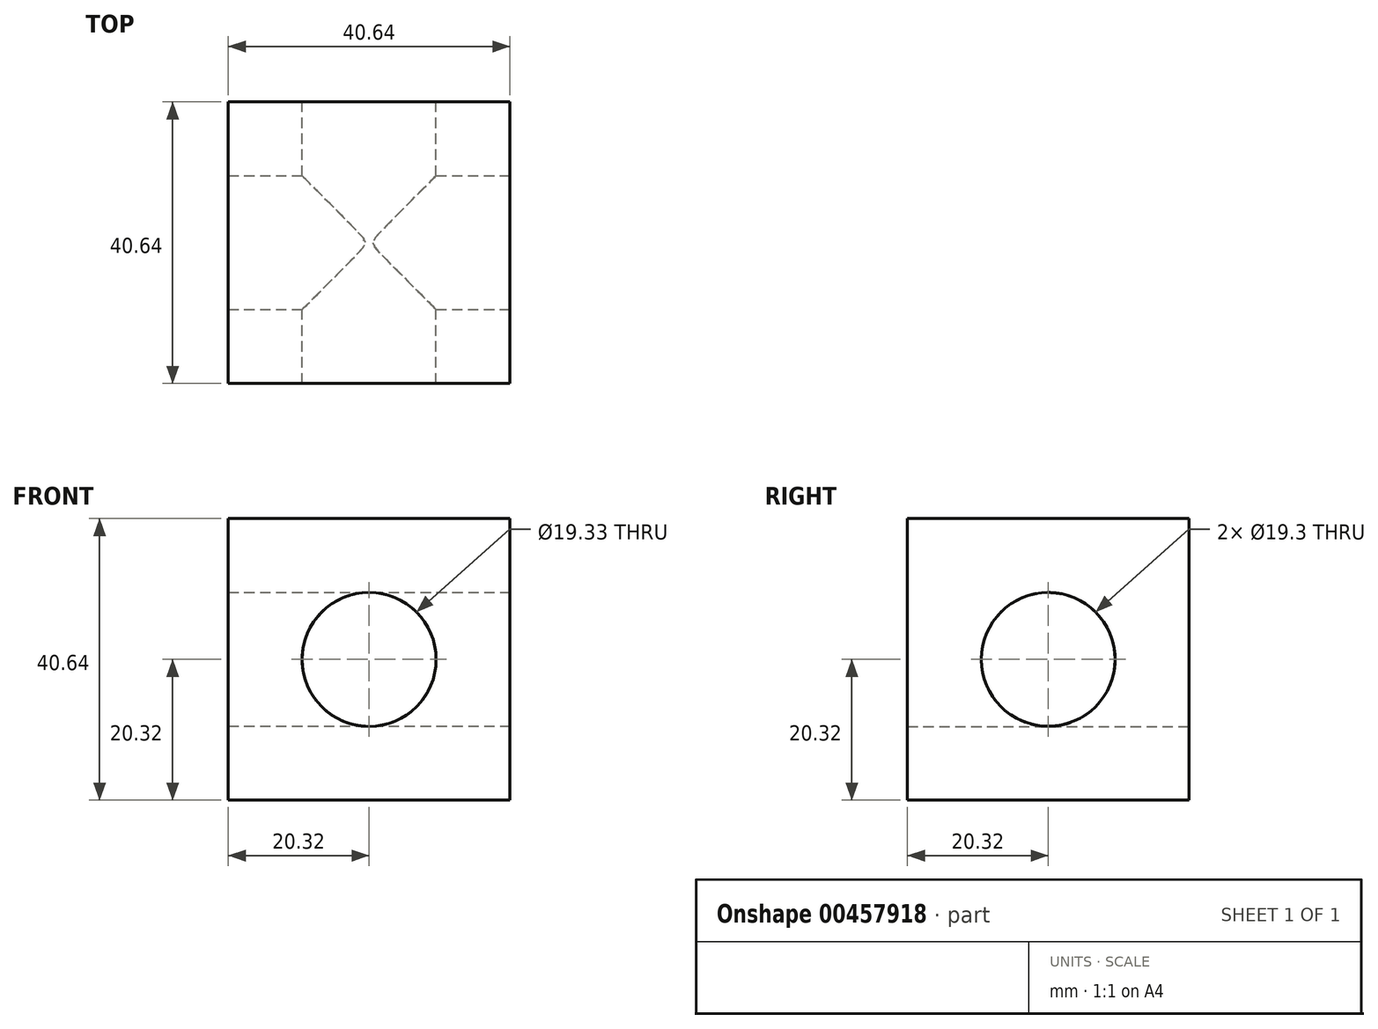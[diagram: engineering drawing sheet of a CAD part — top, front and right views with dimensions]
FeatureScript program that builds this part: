
annotation { "Feature Type Name" : "Feature", "Feature Type Description" : "" }
export const myFeature = defineFeature(function(context is Context, id is Id, definition is map)
    precondition{}
    {
        {
            var Q0;
            Q0=qCreatedBy(makeId("Front.planeOp"),FACE);
            var sketch = newSketch(context, id + "F0", { "sketchPlane" : qUnion([Q0])});
            skLineSegment(sketch, "E0.bottom", {"start": v(0, 0) * mm, "end": v(-40.64, 0) * mm});
            skLineSegment(sketch, "E0.top", {"start": v(0, 40.64) * mm, "end": v(-40.64, 40.64) * mm});
            skLineSegment(sketch, "E0.left", {"start": v(0, 0) * mm, "end": v(0, 40.64) * mm});
            skLineSegment(sketch, "E0.right", {"start": v(-40.64, 0) * mm, "end": v(-40.64, 40.64) * mm});
            skLineSegment(sketch, "E1", {"start": v(-20.32, 40.64) * mm, "end": v(-20.32, 0) * mm, "construction": true});
            skCircle(sketch, "E2", {"center": v(-20.32, 20.32) * mm, "radius": 9.65 * mm, "construction": true});
            skCircle(sketch, "E3", {"center": v(-20.32, 20.32) * mm, "radius": 9.67 * mm});
            skSolve(sketch);
        }
        {
            var Q0;
            Q0 = qSketchRegion(id + "F0", true);
            extrude(context, id + "F1", {"entities" : qUnion([Q0]), "depth" : 40.64 * mm});
        }
        {
            var Q0;
            Q0=makeQuery(id+"F1.opExtrude","SWEPT_FACE",FACE,{"disambiguationData":[OSD([sQuery(id+"F0.wireOp",EDGE,"E0.left")])]});
            var sketch = newSketch(context, id + "F2", { "sketchPlane" : qUnion([Q0])});
            skLineSegment(sketch, "E4", {"start": v(-20.32, 40.64) * mm, "end": v(-20.32, 0) * mm, "construction": true});
            skCircle(sketch, "E5", {"center": v(-20.32, 20.32) * mm, "radius": 9.65 * mm});
            skSolve(sketch);
        }
        {
            var Q0;
            Q0 = qSketchRegion(id + "F2", true);
            var Q1;
            Q1=makeQuery(id+"F1.opExtrude","SWEPT_FACE",FACE,{"disambiguationData":[OSD([sQuery(id+"F0.wireOp",EDGE,"E0.left")])]});
            extrude(context, id + "F3", {"entities" : qUnion([Q0]), "operationType" : NewBodyOperationType.REMOVE, "endBound" : BoundingType.THROUGH_ALL, "oppositeDirection" : true, "endBoundEntityFace" : qUnion([Q1]), "depth" : 25.4 * mm});
        }
    });
